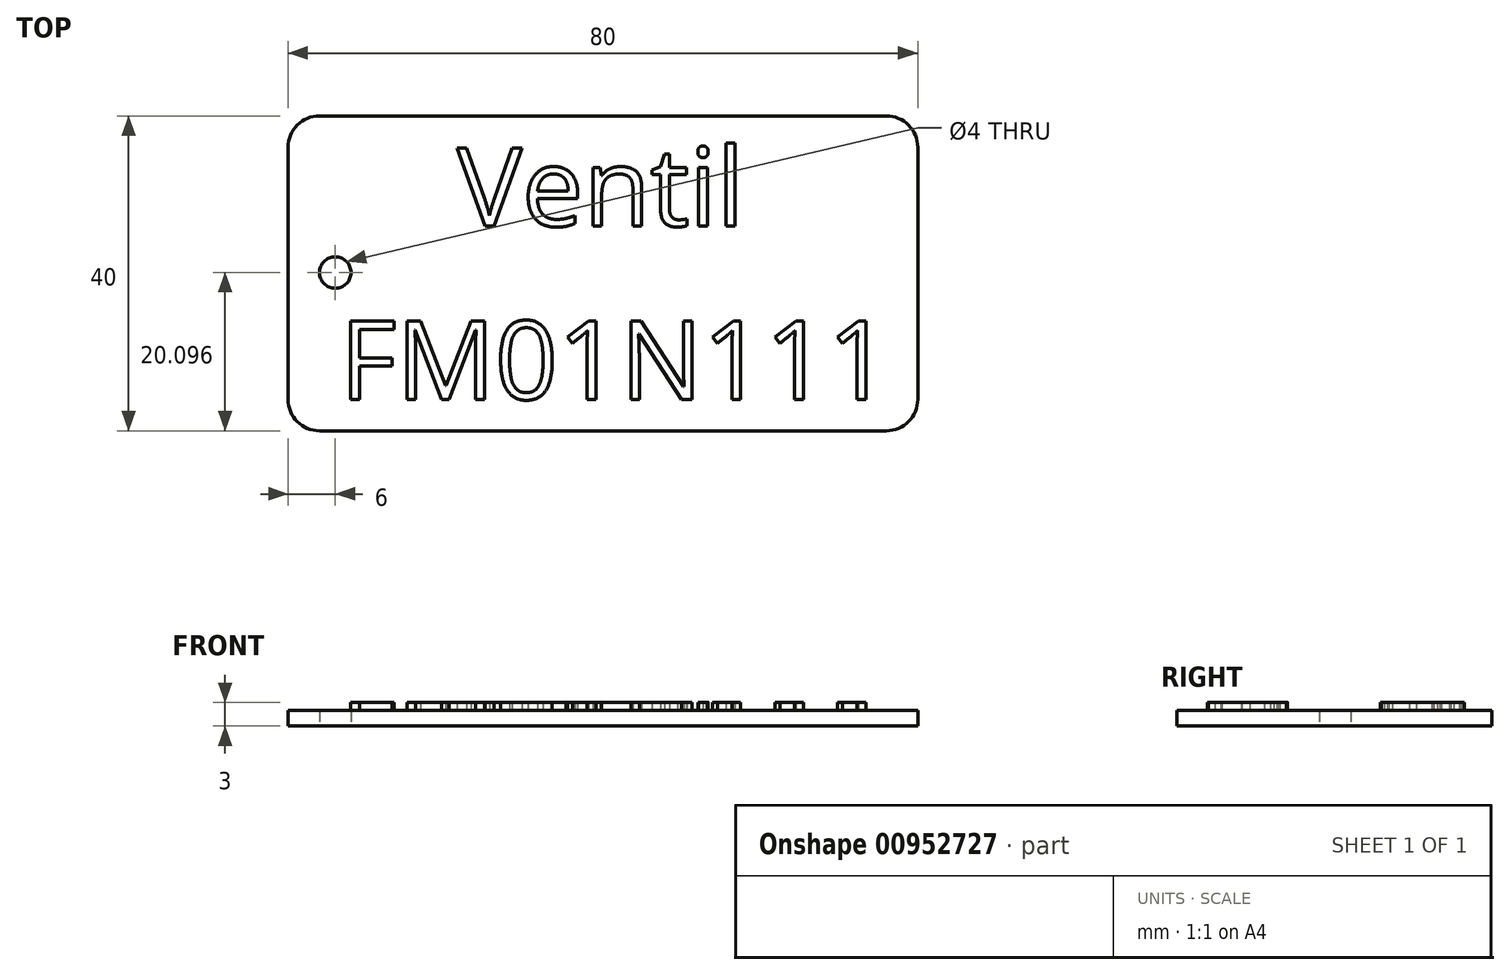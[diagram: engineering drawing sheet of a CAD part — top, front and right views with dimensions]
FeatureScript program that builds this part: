
annotation { "Feature Type Name" : "Feature", "Feature Type Description" : "" }
export const myFeature = defineFeature(function(context is Context, id is Id, definition is map)
    precondition{}
    {
        {
            var Q0;
            Q0=qCreatedBy(makeId("Top.planeOp"),FACE);
            var sketch = newSketch(context, id + "F0", { "sketchPlane" : qUnion([Q0])});
            skLineSegment(sketch, "E0.bottom", {"start": v(36, -20) * mm, "end": v(-36, -20) * mm});
            skLineSegment(sketch, "E0.top", {"start": v(36, 20) * mm, "end": v(-36, 20) * mm});
            skLineSegment(sketch, "E0.left", {"start": v(40, -16) * mm, "end": v(40, 16) * mm});
            skLineSegment(sketch, "E0.right", {"start": v(-40, -16) * mm, "end": v(-40, 16) * mm});
            skPoint(sketch, "E0.middle", {"position": v(0, 0) * mm});
            skPoint(sketch, "E1.visualSharp", {"position": v(40, -20) * mm});
            skArc(sketch, "E1.filletArc", {"start": v(36, -20) * mm, "mid": v(38.83, -18.83) * mm, "end": v(40, -16) * mm});
            skPoint(sketch, "E2.visualSharp", {"position": v(-40, -20) * mm});
            skArc(sketch, "E2.filletArc", {"start": v(-40, -16) * mm, "mid": v(-38.83, -18.83) * mm, "end": v(-36, -20) * mm});
            skPoint(sketch, "E3.visualSharp", {"position": v(40, 20) * mm});
            skArc(sketch, "E3.filletArc", {"start": v(40, 16) * mm, "mid": v(38.83, 18.83) * mm, "end": v(36, 20) * mm});
            skPoint(sketch, "E4.visualSharp", {"position": v(-40, 20) * mm});
            skArc(sketch, "E4.filletArc", {"start": v(-36, 20) * mm, "mid": v(-38.83, 18.83) * mm, "end": v(-40, 16) * mm});
            skLineSegment(sketch, "E5", {"start": v(36, -20) * mm, "end": v(36, 20) * mm, "construction": true});
            skLineSegment(sketch, "E6", {"start": v(-36, -20) * mm, "end": v(-36, 20) * mm, "construction": true});
            skLineSegment(sketch, "E7", {"start": v(-40, -16) * mm, "end": v(40, -16) * mm, "construction": true});
            skLineSegment(sketch, "E8", {"start": v(-40, 16) * mm, "end": v(40, 16) * mm, "construction": true});
            skLineSegment(sketch, "E9", {"start": v(36, 0) * mm, "end": v(-40, 0) * mm});
            skLineSegment(sketch, "E10", {"start": v(36, 0) * mm, "end": v(40, 0) * mm, "construction": true});
            skPoint(sketch, "E11.second.point", {"position": v(-31.11, 0) * mm});
            skPoint(sketch, "E11.third.point", {"position": v(34.69, -1.86) * mm});
            skLineSegment(sketch, "E12.0", {"start": v(-32, -20) * mm, "end": v(-32, 20) * mm, "construction": true});
            skLineSegment(sketch, "E13.0", {"start": v(36, 4) * mm, "end": v(-40, 4) * mm, "construction": true});
            skLineSegment(sketch, "E14.0", {"start": v(36, -4) * mm, "end": v(-40, -4) * mm, "construction": true});
            skCircle(sketch, "E15", {"center": v(-34, 0.1) * mm, "radius": 2 * mm});
            skPoint(sketch, "E15.first.point", {"position": v(-36, 0) * mm});
            skPoint(sketch, "E15.second.point", {"position": v(-32, 0) * mm});
            skPoint(sketch, "E15.third.point", {"position": v(-33.67, 2.07) * mm});
            skSolve(sketch);
        }
        {
            var Q0;
            Q0 = qSketchRegion(id + "F0", true);
            extrude(context, id + "F1", {"entities" : qUnion([Q0]), "depth" : 2 * mm, "offsetDistance" : 25.4 * mm});
        }
        {
            var Q0;
            Q0=makeQuery(id+"F1.opExtrude","CAP_FACE",FACE,{"disambiguationData":[OSD([sQuery(id+"F0.wireOp",EDGE,"E0.bottom"),sQuery(id+"F0.wireOp",EDGE,"E0.top"),sQuery(id+"F0.wireOp",EDGE,"E0.left"),sQuery(id+"F0.wireOp",EDGE,"E0.right"),sQuery(id+"F0.wireOp",EDGE,"E1.filletArc"),sQuery(id+"F0.wireOp",EDGE,"E2.filletArc"),sQuery(id+"F0.wireOp",EDGE,"E3.filletArc"),sQuery(id+"F0.wireOp",EDGE,"E4.filletArc"),sQuery(id+"F0.wireOp",EDGE,"E15")])],"isStart":false});
            var sketch = newSketch(context, id + "F2", { "sketchPlane" : qUnion([Q0])});
            skLineSegment(sketch, "E16", {"start": v(-40, 16) * mm, "end": v(40, 16) * mm, "construction": true});
            skLineSegment(sketch, "E17", {"start": v(-40, -16) * mm, "end": v(40, -16) * mm, "construction": true});
            skLineSegment(sketch, "E18", {"start": v(-39.18, 0) * mm, "end": v(40, 0) * mm, "construction": true});
            skPoint(sketch, "E18.startSnap0", {"position": v(-40, 0) * mm});
            skLineSegment(sketch, "E19.0", {"start": v(-39.18, -4) * mm, "end": v(40, -4) * mm, "construction": true});
            skLineSegment(sketch, "E20.0", {"start": v(-39.18, 4) * mm, "end": v(40, 4) * mm, "construction": true});
            skLineSegment(sketch, "E21.0", {"start": v(-40, -6) * mm, "end": v(40, -6) * mm, "construction": true});
            skLineSegment(sketch, "E22.0", {"start": v(-40, 6) * mm, "end": v(40, 6) * mm, "construction": true});
            skText(sketch, "E23", { "text": "Ventil", "fontName": "OpenSans-Regular.ttf"});
            skText(sketch, "E24", { "text": "FM01N111", "fontName": "OpenSans-Regular.ttf"});
            const initialGuessF2  = {"E23": [-0.01854, 0.006, 1, 0, 0.01], "E24": [-0.0334, -0.016, 1, 0, 0.01]};
            skSetInitialGuess(sketch, initialGuessF2);
            skSolve(sketch);
        }
        {
            var Q0;
            Q0 = qSketchRegion(id + "F2", true);
            extrude(context, id + "F3", {"entities" : qUnion([Q0]), "operationType" : NewBodyOperationType.ADD, "depth" : 1 * mm, "offsetDistance" : 25.4 * mm});
        }
    });
